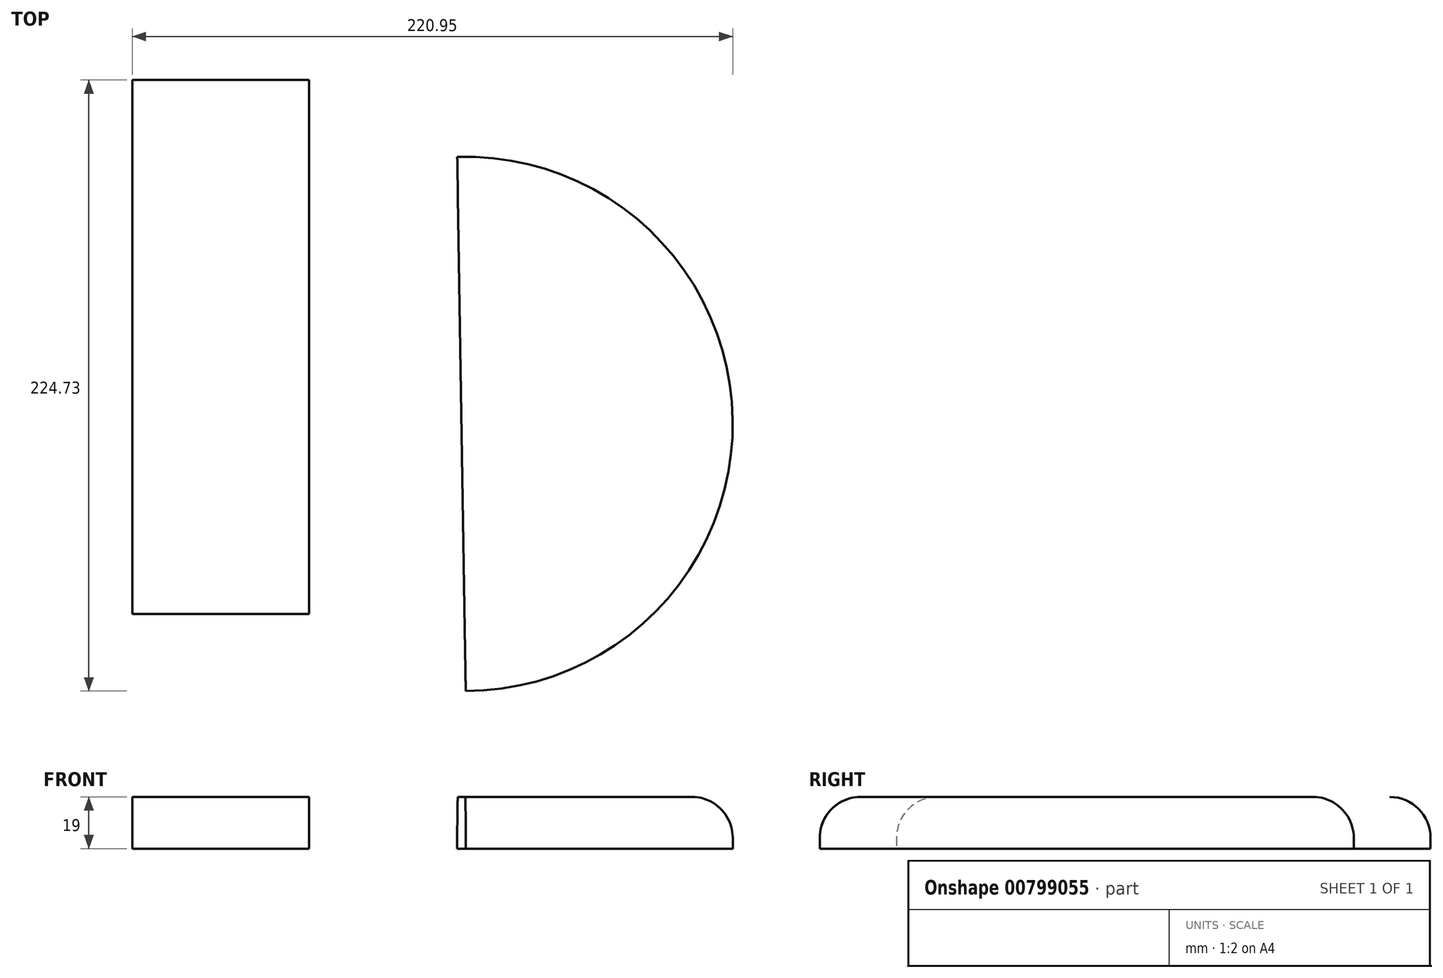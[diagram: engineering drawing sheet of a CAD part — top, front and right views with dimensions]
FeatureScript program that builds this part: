
annotation { "Feature Type Name" : "Feature", "Feature Type Description" : "" }
export const myFeature = defineFeature(function(context is Context, id is Id, definition is map)
    precondition{}
    {
        {
            var Q0;
            Q0=qCreatedBy(makeId("Top.planeOp"),FACE);
            var sketch = newSketch(context, id + "F0", { "sketchPlane" : qUnion([Q0])});
            skLineSegment(sketch, "E0", {"start": v(-3.12, 98.2) * mm, "end": v(0, -98.25) * mm});
            skArc(sketch, "E1", {"start": v(0, -98.25) * mm, "mid": v(98.23, 1.56) * mm, "end": v(-3.12, 98.2) * mm});
            skSolve(sketch);
        }
        {
            var Q0;
            Q0 = qSketchRegion(id + "F0", true);
            extrude(context, id + "F1", {"entities" : qUnion([Q0]), "depth" : 19 * mm, "offsetDistance" : 25 * mm});
        }
        {
            var Q0;
            Q0=qCreatedBy(makeId("Top.planeOp"),FACE);
            var sketch = newSketch(context, id + "F2", { "sketchPlane" : qUnion([Q0])});
            skLineSegment(sketch, "E2.bottom", {"start": v(-57.7, 126.48) * mm, "end": v(-122.7, 126.48) * mm});
            skLineSegment(sketch, "E2.top", {"start": v(-57.7, -69.98) * mm, "end": v(-122.7, -69.98) * mm});
            skLineSegment(sketch, "E2.left", {"start": v(-57.7, 126.48) * mm, "end": v(-57.7, -69.98) * mm});
            skLineSegment(sketch, "E2.right", {"start": v(-122.7, 126.48) * mm, "end": v(-122.7, -69.98) * mm});
            skSolve(sketch);
        }
        {
            var Q0;
            Q0 = qSketchRegion(id + "F2", true);
            extrude(context, id + "F3", {"entities" : qUnion([Q0]), "depth" : 19 * mm, "offsetDistance" : 25 * mm});
        }
        {
            var Q0;
            Q0=makeQuery(id+"F3.opExtrude","CAP_EDGE",EDGE,{"disambiguationData":[OSD([sQuery(id+"F2.wireOp",EDGE,"E2.bottom")])],"isStart":false});
            var Q1;
            Q1=makeQuery(id+"F3.opExtrude","CAP_EDGE",EDGE,{"disambiguationData":[OSD([sQuery(id+"F2.wireOp",EDGE,"E2.top")])],"isStart":false});
            var Q2;
            Q2=makeQuery(id+"F1.opExtrude","CAP_EDGE",EDGE,{"disambiguationData":[OSD([sQuery(id+"F0.wireOp",EDGE,"E1")])],"isStart":false});
            fillet(context, id + "F4", {"entities" : qUnion([Q0, Q1, Q2]), "radius" : 15 * mm, "tangentPropagation" : true, "allowEdgeOverflow" : false});
        }
    });
